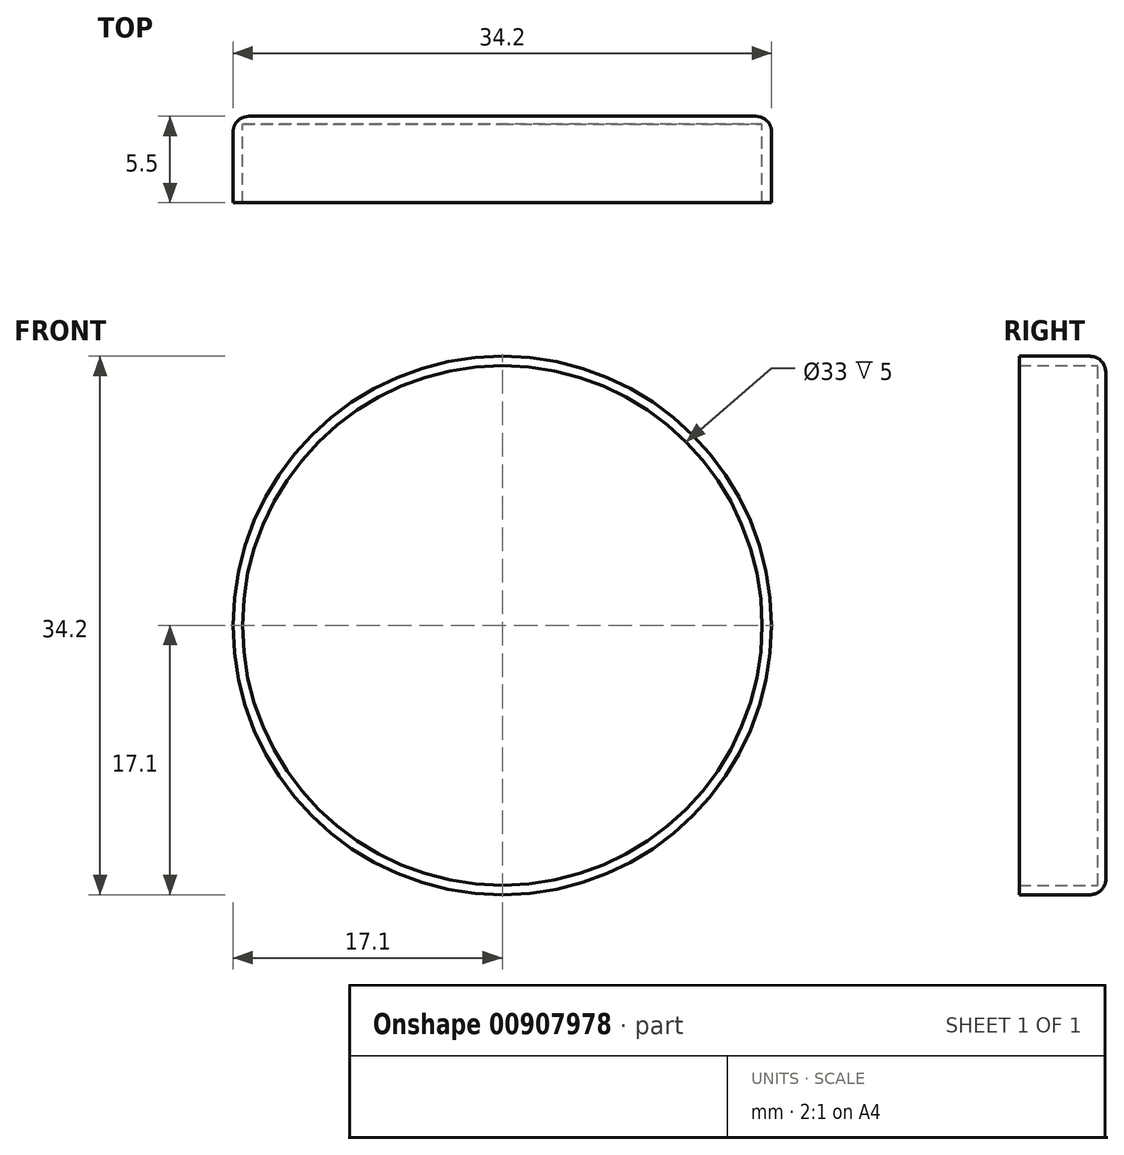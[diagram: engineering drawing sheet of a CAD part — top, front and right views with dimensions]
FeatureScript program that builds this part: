
annotation { "Feature Type Name" : "Feature", "Feature Type Description" : "" }
export const myFeature = defineFeature(function(context is Context, id is Id, definition is map)
    precondition{}
    {
        {
            var Q0;
            Q0=qCreatedBy(makeId("Front.planeOp"),FACE);
            var sketch = newSketch(context, id + "F0", { "sketchPlane" : qUnion([Q0])});
            skCircle(sketch, "E0", {"center": v(0, 0) * mm, "radius": 16.5 * mm});
            skCircle(sketch, "E1", {"center": v(0, 0) * mm, "radius": 17.1 * mm});
            skSolve(sketch);
        }
        {
            var Q0;
            Q0 = qSketchRegion(id + "F0", true);
            extrude(context, id + "F1", {"entities" : qUnion([Q0]), "depth" : 5.5 * mm, "offsetDistance" : 25 * mm});
        }
        {
            var Q0;
            Q0=makeQuery(id+"F0.imprint","IMPRINT",FACE,{"disambiguationData":[TD([[makeQuery(id+"F0.imprint","IMPRINT",EDGE,{"derivedFrom":sQuery(id+"F0.wireOp",EDGE,"E0")}),1.0]])]});
            extrude(context, id + "F2", {"entities" : qUnion([Q0]), "operationType" : NewBodyOperationType.ADD, "depth" : .5 * mm, "offsetDistance" : 25 * mm});
        }
        {
            var Q0;
            Q0=makeQuery(id+"F1.opExtrude","CAP_EDGE",EDGE,{"disambiguationData":[OSD([sQuery(id+"F0.wireOp",EDGE,"E1")])],"isStart":true});
            fillet(context, id + "F3", {"entities" : qUnion([Q0]), "radius" : 1 * mm, "tangentPropagation" : true, "allowEdgeOverflow" : false});
        }
    });
